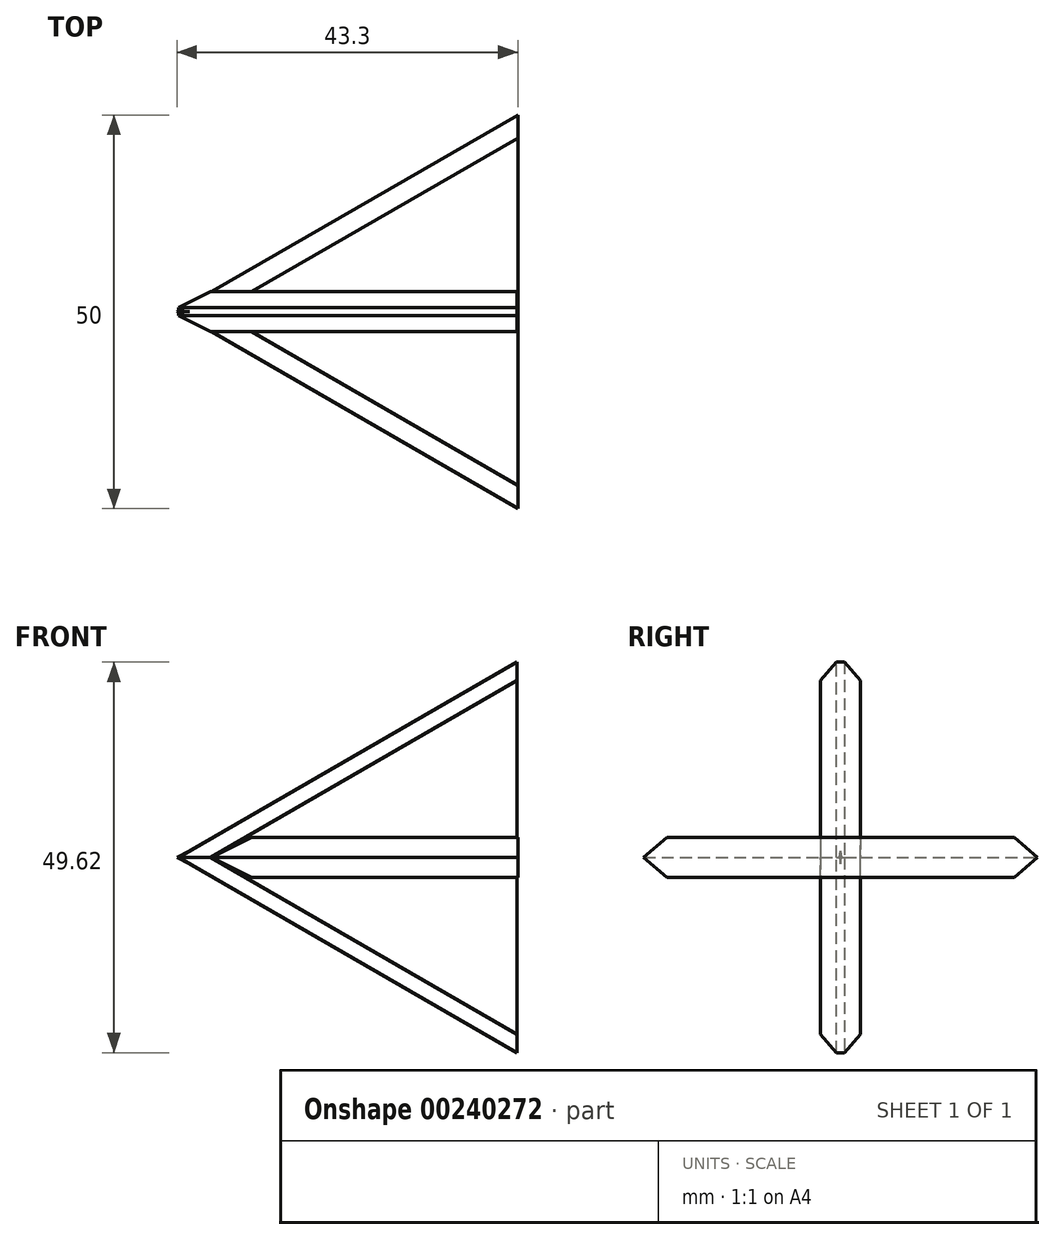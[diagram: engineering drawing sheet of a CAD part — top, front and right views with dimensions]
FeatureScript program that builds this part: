
annotation { "Feature Type Name" : "Feature", "Feature Type Description" : "" }
export const myFeature = defineFeature(function(context is Context, id is Id, definition is map)
    precondition{}
    {
        {
            var Q0;
            Q0=qCreatedBy(makeId("Top.planeOp"),FACE);
            var sketch = newSketch(context, id + "F0", { "sketchPlane" : qUnion([Q0])});
            skCircle(sketch, "E0.cCircle", {"center": v(0, 0) * mm, "radius": 14.43 * mm, "construction": true});
            skLineSegment(sketch, "E0.0", {"start": v(14.43, 25) * mm, "end": v(14.43, -25) * mm});
            skLineSegment(sketch, "E0.1", {"start": v(14.43, -25) * mm, "end": v(-28.87, 0) * mm});
            skLineSegment(sketch, "E0.2", {"start": v(-28.87, 0) * mm, "end": v(14.43, 25) * mm});
            skPoint(sketch, "E0.0.midPoint", {"position": v(14.43, 0) * mm});
            skSolve(sketch);
        }
        {
            var Q0;
            Q0 = qSketchRegion(id + "F0", true);
            extrude(context, id + "F1", {"entities" : qUnion([Q0]), "endBound" : BoundingType.SYMMETRIC, "depth" : 5.08 * mm});
        }
        {
            var Q0;
            Q0=makeQuery(id+"F1.opExtrude","CAP_EDGE",EDGE,{"disambiguationData":[OSD([sQuery(id+"F0.wireOp",EDGE,"E0.2")])],"isStart":false});
            var Q1;
            Q1=makeQuery(id+"F1.opExtrude","CAP_EDGE",EDGE,{"disambiguationData":[OSD([sQuery(id+"F0.wireOp",EDGE,"E0.1")])],"isStart":false});
            var Q2;
            Q2=makeQuery(id+"F1.opExtrude","CAP_EDGE",EDGE,{"disambiguationData":[OSD([sQuery(id+"F0.wireOp",EDGE,"E0.1")])],"isStart":true});
            var Q3;
            Q3=makeQuery(id+"F1.opExtrude","CAP_EDGE",EDGE,{"disambiguationData":[OSD([sQuery(id+"F0.wireOp",EDGE,"E0.2")])],"isStart":true});
            chamfer(context, id + "F2", {"entities" : qUnion([Q0, Q1, Q2, Q3]), "width" : 2.54 * mm, "tangentPropagation" : true});
        }
        {
            var Q0;
            Q0=qCreatedBy(makeId("Front.planeOp"),FACE);
            var sketch = newSketch(context, id + "F3", { "sketchPlane" : qUnion([Q0])});
            skCircle(sketch, "E1.cCircle", {"center": v(0, 0) * mm, "radius": 14.32 * mm, "construction": true});
            skLineSegment(sketch, "E1.0", {"start": v(14.32, 24.81) * mm, "end": v(14.32, -24.81) * mm});
            skLineSegment(sketch, "E1.1", {"start": v(14.32, -24.81) * mm, "end": v(-28.65, 0) * mm});
            skLineSegment(sketch, "E1.2", {"start": v(-28.65, 0) * mm, "end": v(14.32, 24.81) * mm});
            skPoint(sketch, "E1.0.midPoint", {"position": v(14.32, 0) * mm});
            skSolve(sketch);
        }
        {
            var Q0;
            Q0=makeQuery(id+"F3.imprint","IMPRINT",FACE,{"disambiguationData":[TD([[makeQuery(id+"F3.imprint","IMPRINT",EDGE,{"derivedFrom":sQuery(id+"F3.wireOp",EDGE,"E1.0")}),-1.0]])]});
            extrude(context, id + "F4", {"entities" : qUnion([Q0]), "operationType" : NewBodyOperationType.ADD, "endBound" : BoundingType.SYMMETRIC, "depth" : 5.08 * mm});
        }
        {
            var Q0;
            Q0=makeQuery(id+"F4.opExtrude","CAP_EDGE",EDGE,{"disambiguationData":[OSD([sQuery(id+"F3.wireOp",EDGE,"E1.2")])],"isStart":true});
            var Q1;
            Q1=makeQuery(id+"F4.opExtrude","CAP_EDGE",EDGE,{"disambiguationData":[OSD([sQuery(id+"F3.wireOp",EDGE,"E1.2")])],"isStart":false});
            var Q2;
            Q2=makeQuery(id+"F4.opExtrude","CAP_EDGE",EDGE,{"disambiguationData":[OSD([sQuery(id+"F3.wireOp",EDGE,"E1.1")])],"isStart":false});
            var Q3;
            Q3=makeQuery(id+"F4.opExtrude","CAP_EDGE",EDGE,{"disambiguationData":[OSD([sQuery(id+"F3.wireOp",EDGE,"E1.1")])],"isStart":true});
            chamfer(context, id + "F5", {"entities" : qUnion([Q0, Q1, Q2, Q3]), "width" : 2.03 * mm, "tangentPropagation" : true});
        }
    });
